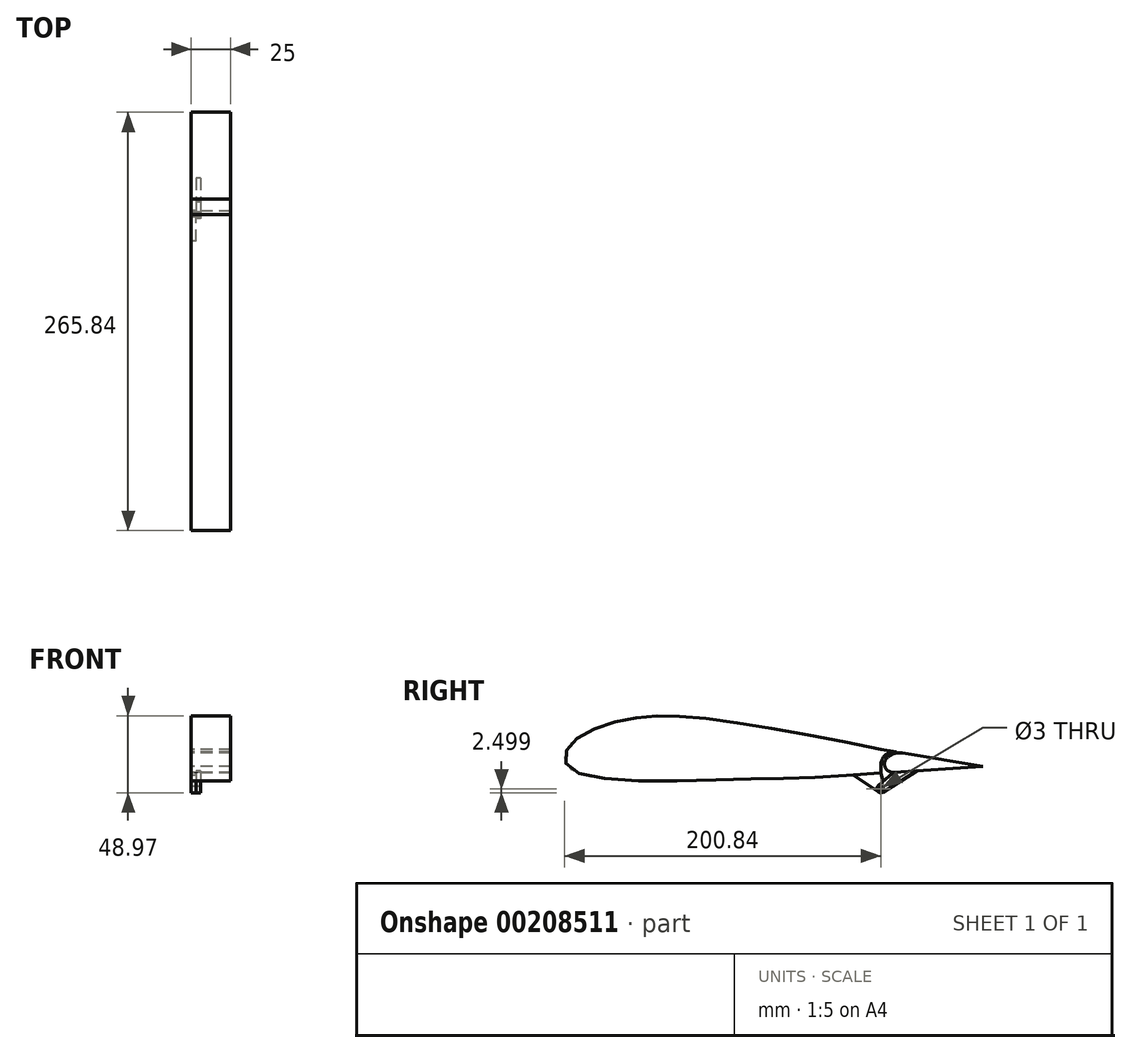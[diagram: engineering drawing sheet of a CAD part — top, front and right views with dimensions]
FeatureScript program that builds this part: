
annotation { "Feature Type Name" : "Feature", "Feature Type Description" : "" }
export const myFeature = defineFeature(function(context is Context, id is Id, definition is map)
    precondition{}
    {
        {
            var Q0;
            Q0=qCreatedBy(makeId("Right.planeOp"),FACE);
            var sketch = newSketch(context, id + "F0", { "sketchPlane" : qUnion([Q0])});
            skLineSegment(sketch, "E0", {"start": v(0, 0) * mm, "end": v(0, 15) * mm});
            skFitSpline(sketch, "E1", {"points": [v(0, 15) * mm, v(-114.81, 35.05) * mm, v(-162.65, 33.87) * mm, v(-197.15, 18.19) * mm, v(-197.93, 3.29) * mm, v(-101.87, -4.16) * mm, v(0, 0) * mm], "startDerivative": vector(-506.44, 105.84) * mm, "endDerivative": vector(524.48, 46.41) * mm});
            skLineSegment(sketch, "E2.0", {"start": v(-3, 2.75) * mm, "end": v(-3, 12.56) * mm});
            skFitSpline(sketch, "E2.1", {"points": [v(-0.61, 12.06) * mm, v(-5.88, 13.16) * mm, v(-16.72, 15.4) * mm, v(-33.48, 18.74) * mm, v(-50.39, 21.97) * mm, v(-67.08, 24.99) * mm, v(-83.2, 27.7) * mm, v(-95.83, 29.62) * mm, v(-105.29, 30.9) * mm, v(-110.88, 31.6) * mm, v(-115.14, 32.07) * mm, v(-119.25, 32.5) * mm, v(-124.13, 32.92) * mm, v(-129.62, 33.27) * mm, v(-136.53, 33.5) * mm, v(-142.95, 33.4) * mm, v(-149.14, 32.94) * mm, v(-153.72, 32.4) * mm, v(-157.55, 31.8) * mm, v(-160.65, 31.22) * mm, v(-163.79, 30.57) * mm, v(-167.77, 29.64) * mm, v(-172.52, 28.3) * mm, v(-177.15, 26.78) * mm, v(-181.56, 25.05) * mm, v(-185.64, 23.13) * mm, v(-189.29, 21.03) * mm, v(-191.87, 19.15) * mm, v(-193.62, 17.59) * mm, v(-194.77, 16.4) * mm, v(-195.74, 15.17) * mm, v(-196.8, 13.54) * mm, v(-197.5, 11.94) * mm, v(-197.8, 10.47) * mm, v(-197.87, 9.45) * mm, v(-197.76, 8.51) * mm, v(-197.5, 7.64) * mm, v(-197.06, 6.79) * mm, v(-196.4, 5.94) * mm, v(-195.48, 5.1) * mm, v(-194.2, 4.24) * mm, v(-192.56, 3.4) * mm, v(-189.96, 2.35) * mm, v(-185.96, 1.2) * mm, v(-180.15, 0.08) * mm, v(-173.49, -0.76) * mm, v(-166.11, -1.36) * mm, v(-155.52, -1.86) * mm, v(-144.04, -1.98) * mm, v(-132.18, -1.87) * mm, v(-123.23, -1.7) * mm, v(-114.33, -1.49) * mm, v(-107.06, -1.3) * mm, v(-101.4, -1.15) * mm, v(-95.86, -1.01) * mm, v(-89.15, -0.86) * mm, v(-81.39, -0.7) * mm, v(-71.36, -0.49) * mm, v(-59.28, -0.22) * mm, v(-45.13, 0.2) * mm, v(-30.89, 0.81) * mm, v(-16.15, 1.69) * mm, v(-5.7, 2.5) * mm, v(-0.26, 2.99) * mm]});
            skSolve(sketch);
        }
        {
            var Q0;
            Q0 = qSketchRegion(id + "F0", true);
            extrude(context, id + "F1", {"entities" : qUnion([Q0]), "depth" : 25 * mm});
        }
        {
            var Q0;
            Q0=qCreatedBy(makeId("Right.planeOp"),FACE);
            var sketch = newSketch(context, id + "F2", { "sketchPlane" : qUnion([Q0])});
            skLineSegment(sketch, "E3", {"start": v(0, 0) * mm, "end": v(0, 15) * mm});
            skLineSegment(sketch, "E4", {"start": v(0, 15) * mm, "end": v(65, 4.19) * mm});
            skLineSegment(sketch, "E5", {"start": v(65, 4.19) * mm, "end": v(0, 0) * mm});
            skSolve(sketch);
        }
        {
            var Q0;
            Q0=makeQuery(id+"F1.opExtrude","CAP_FACE",FACE,{"disambiguationData":[OSD([sQuery(id+"F0.wireOp",EDGE,"E0"),sQuery(id+"F0.wireOp",EDGE,"E1"),sQuery(id+"F0.wireOp",EDGE,"E2.0"),sQuery(id+"F0.wireOp",EDGE,"E2.1")])],"isStart":true});
            var sketch = newSketch(context, id + "F3", { "sketchPlane" : qUnion([Q0])});
            skLineSegment(sketch, "E6", {"start": v(0, 0) * mm, "end": v(0, 5) * mm});
            skArc(sketch, "E7", {"start": v(0, 5) * mm, "mid": v(-3, 11.47) * mm, "end": v(-9.86, 13.36) * mm});
            skLineSegment(sketch, "E8", {"start": v(-9.86, 13.36) * mm, "end": v(0, 15) * mm});
            skLineSegment(sketch, "E9", {"start": v(0, 15) * mm, "end": v(0, 5) * mm});
            skSolve(sketch);
        }
        {
            var Q0;
            Q0 = qSketchRegion(id + "F3", true);
            extrude(context, id + "F4", {"entities" : qUnion([Q0]), "operationType" : NewBodyOperationType.ADD, "oppositeDirection" : true, "depth" : 25 * mm});
        }
        {
            var Q0;
            Q0=makeQuery(id+"F2.imprint","IMPRINT",FACE,{"disambiguationData":[TD([[makeQuery(id+"F2.imprint","IMPRINT",EDGE,{"derivedFrom":sQuery(id+"F2.wireOp",EDGE,"E3")}),-1.0]])]});
            var sketch = newSketch(context, id + "F5", { "sketchPlane" : qUnion([Q0])});
            skLineSegment(sketch, "E10", {"start": v(13.7, 12.72) * mm, "end": v(65, 4.19) * mm});
            skLineSegment(sketch, "E11", {"start": v(65, 4.19) * mm, "end": v(8, 0.52) * mm});
            skCircle(sketch, "E12", {"center": v(8.47, 5) * mm, "radius": 6.5 * mm});
            skArc(sketch, "E13", {"start": v(13.7, 12.72) * mm, "mid": v(8.45, 12.35) * mm, "end": v(3.93, 9.65) * mm});
            skArc(sketch, "E14", {"start": v(3.93, 9.65) * mm, "mid": v(2.79, 3.67) * mm, "end": v(8, 0.52) * mm});
            skSolve(sketch);
        }
        {
            var Q0;
            {var subQ0=sQuery(id+"F5.wireOp",EDGE,"E10");Q0=makeQuery(id+"F5.imprint","IMPRINT",FACE,{"disambiguationData":[TD([[makeQuery(id+"F5.imprint","IMPRINT",EDGE,{"derivedFrom":subQ0}),-1.0]])]});}
            var Q1;
            {var subQ0=sQuery(id+"F5.wireOp",EDGE,"E14");Q1=makeQuery(id+"F5.imprint","IMPRINT",FACE,{"disambiguationData":[TD([[makeQuery(id+"F5.imprint","IMPRINT",EDGE,{"derivedFrom":subQ0}),1.0]])]});}
            extrude(context, id + "F6", {"entities" : qUnion([Q0, Q1]), "depth" : 25 * mm});
        }
        {
            var Q0;
            Q0=makeQuery(id+"F6.opExtrude","CAP_FACE",FACE,{"disambiguationData":[OSD([sQuery(id+"F5.wireOp",EDGE,"E10"),sQuery(id+"F5.wireOp",EDGE,"E11"),sQuery(id+"F5.wireOp",EDGE,"E13"),sQuery(id+"F5.wireOp",EDGE,"E14")])],"isStart":true});
            var sketch = newSketch(context, id + "F7", { "sketchPlane" : qUnion([Q0])});
            skLineSegment(sketch, "E15", {"start": v(-23, 1.48) * mm, "end": v(-1.33, -12.14) * mm});
            skLineSegment(sketch, "E16", {"start": v(-8, 0.52) * mm, "end": v(1.67, -8.16) * mm});
            skCircle(sketch, "E17", {"center": v(0, -10.02) * mm, "radius": 2.5 * mm});
            skCircle(sketch, "E18", {"center": v(0, -10.02) * mm, "radius": 1.5 * mm});
            skSolve(sketch);
        }
        {
            var Q0;
            {var subQ0=sQuery(id+"F7.wireOp",EDGE,"E15");Q0=makeQuery(id+"F7.imprint","IMPRINT",FACE,{"disambiguationData":[TD([[makeQuery(id+"F7.imprint","IMPRINT",EDGE,{"derivedFrom":subQ0}),1.0]])]});}
            var Q1;
            Q1=makeQuery(id+"F7.imprint","IMPRINT",FACE,{"disambiguationData":[TD([[makeQuery(id+"F7.imprint","IMPRINT",EDGE,{"derivedFrom":sQuery(id+"F7.wireOp",EDGE,"E18")}),-1.0]])]});
            extrude(context, id + "F8", {"entities" : qUnion([Q0, Q1]), "operationType" : NewBodyOperationType.ADD, "oppositeDirection" : true, "depth" : 6 * mm, "hasSecondDirection" : true, "secondDirectionOppositeDirection" : true, "secondDirectionDepth" : 3 * mm});
        }
        {
            var Q0;
            Q0=makeQuery(id+"F4.boolean.opBoolean","MERGE",FACE,{"derivedFrom":[makeQuery(id+"F1.opExtrude","CAP_FACE",FACE,{"disambiguationData":[OSD([sQuery(id+"F0.wireOp",EDGE,"E0"),sQuery(id+"F0.wireOp",EDGE,"E1"),sQuery(id+"F0.wireOp",EDGE,"E2.0"),sQuery(id+"F0.wireOp",EDGE,"E2.1")])],"isStart":true}),makeQuery(id+"F4.opExtrude","CAP_FACE",FACE,{"disambiguationData":[OSD([sQuery(id+"F3.wireOp",EDGE,"E7"),sQuery(id+"F3.wireOp",EDGE,"E8"),sQuery(id+"F3.wireOp",EDGE,"E9")])],"isStart":true})]});
            var sketch = newSketch(context, id + "F9", { "sketchPlane" : qUnion([Q0])});
            skCircle(sketch, "E19", {"center": v(0, -10.02) * mm, "radius": 1.5 * mm});
            skCircle(sketch, "E20", {"center": v(0, -10.02) * mm, "radius": 2.5 * mm});
            skLineSegment(sketch, "E21", {"start": v(-2.42, -9.4) * mm, "end": v(0, 0) * mm});
            skLineSegment(sketch, "E22", {"start": v(0, 0) * mm, "end": v(16.91, -1.32) * mm});
            skLineSegment(sketch, "E23", {"start": v(16.91, -1.32) * mm, "end": v(1.43, -12.07) * mm});
            skSolve(sketch);
        }
        {
            var Q0;
            {var subQ0=sQuery(id+"F9.wireOp",EDGE,"E23");Q0=makeQuery(id+"F9.imprint","IMPRINT",FACE,{"disambiguationData":[TD([[makeQuery(id+"F9.imprint","IMPRINT",EDGE,{"derivedFrom":subQ0}),-1.0]])]});}
            var Q1;
            Q1=makeQuery(id+"F9.imprint","IMPRINT",FACE,{"disambiguationData":[TD([[makeQuery(id+"F9.imprint","IMPRINT",EDGE,{"derivedFrom":sQuery(id+"F9.wireOp",EDGE,"E19")}),-1.0]])]});
            extrude(context, id + "F10", {"entities" : qUnion([Q0, Q1]), "operationType" : NewBodyOperationType.ADD, "oppositeDirection" : true, "depth" : 3 * mm});
        }
    });
